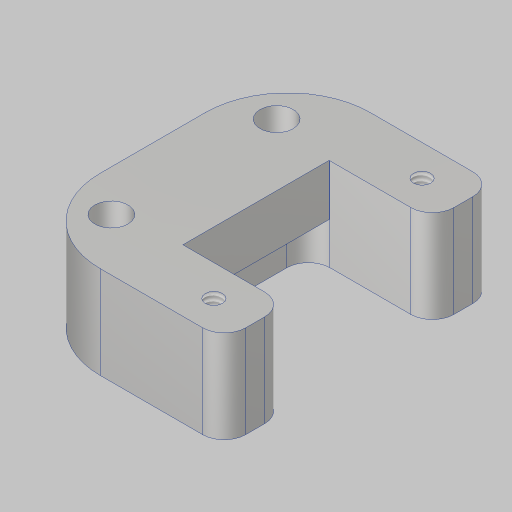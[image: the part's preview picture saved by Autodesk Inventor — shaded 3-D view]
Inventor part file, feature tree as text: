
AUTODESK INVENTOR PART (.ipt)
format: ipt  version: 2023.5 (Build 275446000, 446)  size: 177,152 bytes
history: native  units: in
note: dims shown in document units (in); Inventor stores cm internally (conversion verified against a paired STEP export)
features: sketch x5, extrude x3, hole x2, fillet x2, projected_geometry x2
ambient origin geometry x8: Origin, YZ Plane, XZ Plane, XY Plane, X Axis, Y Axis, Z Axis, Center Point
bodies: Solid1 (feature_tree)
feature tree (14):
  extrude  "Extrusion1"  Depth=0.31in
  hole  "Hole1"  [1 undecoded]
  extrude  "Extrusion2"  Depth=0.25in
  extrude  "Extrusion3"  Depth=0.75in
  hole  "Hole3"  [1 undecoded]
  fillet  "Fillet1"  Radius=0.25in
  fillet  "Fillet2"  Radius=1.0in
  sketch  "Sketch1"  dims[d1=1.2598in d2=0.31in]
  sketch  "Sketch2"  dims[d4=0.25in d5=0.375in]
  sketch  "Sketch4"  dims[d6=1.25in d7=0.0in d8=0.25in]
  sketch  "Sketch5"  dims[d9=0.104in d10=0.276in d11=0.375in d12=0.25in d13=0.5635in d14=1.0in d15=0.8108in d25=0.75in]
  sketch  "Sketch6"  dims[d26=1.5in d27=0.0in d28=1.5in d29=0.0in d30=0.25in d31=1.0in d32=0.201in d33=0.75in d34=0.375in d35=0.25in d36=0.5635in d37=1.0in d38=0.8108in d39=0.5in d40=0.13in d41=0.5in d42=0.0344in]
  projected_geometry  "Project Cut Edges1"
  projected_geometry  "Project Cut Edges2"
note: 2 required parameter values undecoded (feature->parameter linkage not recoverable at this tier; creation-order binding heuristic only, values carry confidence <= 0.55)
